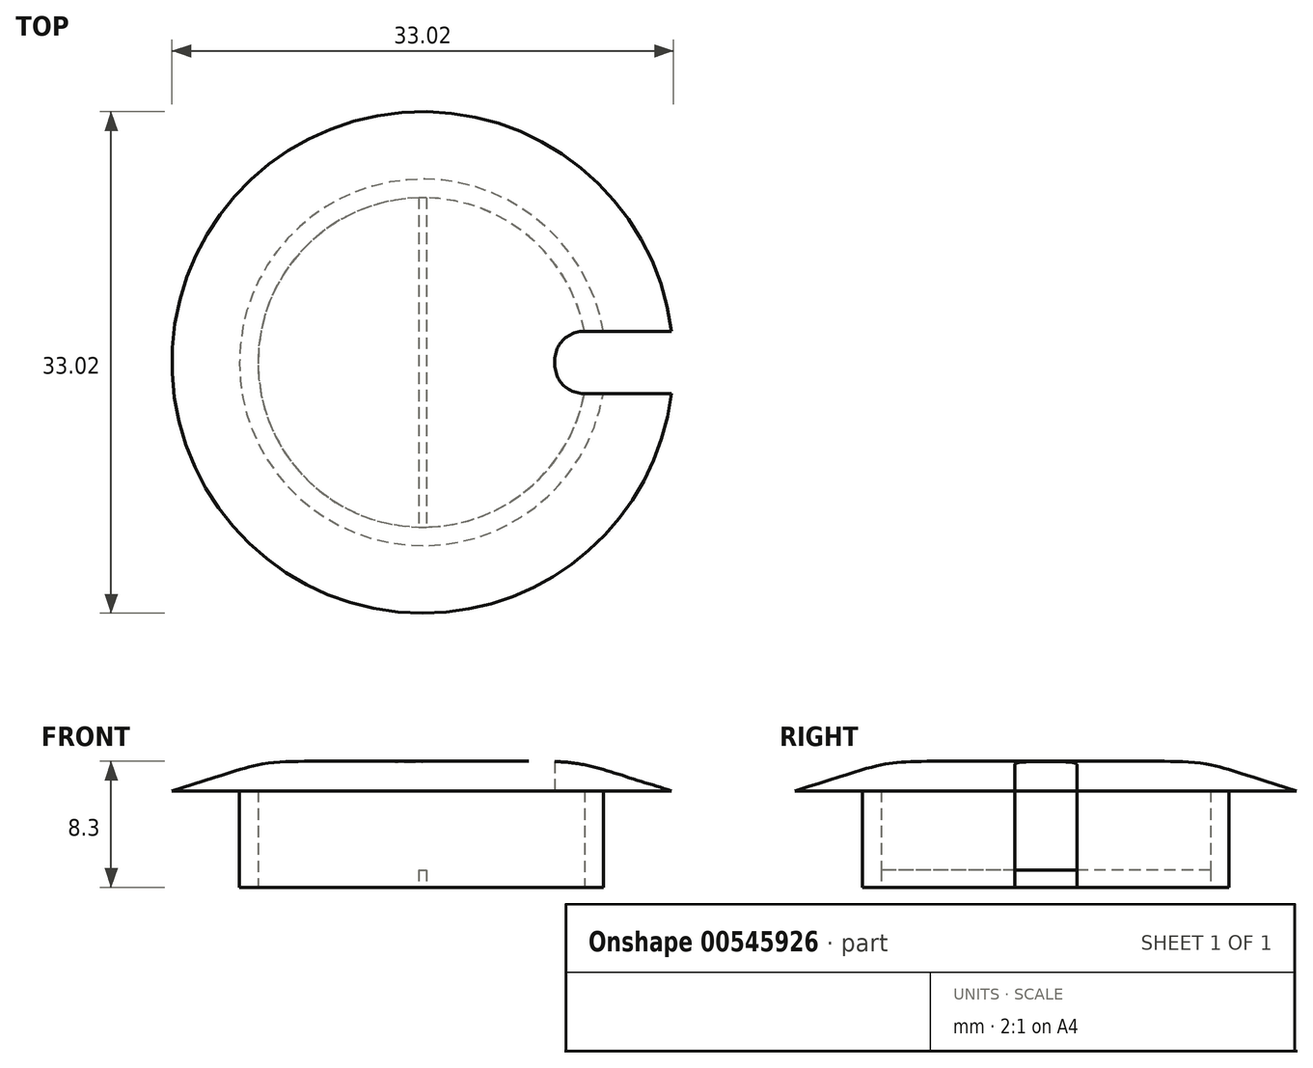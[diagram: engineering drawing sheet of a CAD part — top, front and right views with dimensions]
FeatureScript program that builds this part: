
annotation { "Feature Type Name" : "Feature", "Feature Type Description" : "" }
export const myFeature = defineFeature(function(context is Context, id is Id, definition is map)
    precondition{}
    {
        {
            var Q0;
            Q0=qCreatedBy(makeId("Top.planeOp"),FACE);
            var sketch = newSketch(context, id + "F0", { "sketchPlane" : qUnion([Q0])});
            skCircle(sketch, "E0", {"center": v(0, 0) * mm, "radius": 12.07 * mm});
            skCircle(sketch, "E1", {"center": v(0, 0) * mm, "radius": 10.85 * mm});
            skSolve(sketch);
        }
        {
            var Q0;
            Q0=makeQuery(id+"F0.imprint","IMPRINT",FACE,{"disambiguationData":[TD([[makeQuery(id+"F0.imprint","IMPRINT",EDGE,{"derivedFrom":sQuery(id+"F0.wireOp",EDGE,"E0")}),1.0]])]});
            extrude(context, id + "F1", {"entities" : qUnion([Q0]), "depth" : 6.35 * mm, "offsetDistance" : 25.4 * mm});
        }
        {
            var Q0;
            Q0=makeQuery(id+"F1.opExtrude","CAP_FACE",FACE,{"disambiguationData":[OSD([sQuery(id+"F0.wireOp",EDGE,"E0"),sQuery(id+"F0.wireOp",EDGE,"E1")])],"isStart":false});
            var sketch = newSketch(context, id + "F2", { "sketchPlane" : qUnion([Q0])});
            skCircle(sketch, "E2", {"center": v(0, 0) * mm, "radius": 15.88 * mm});
            skSolve(sketch);
        }
        {
            var Q0;
            Q0=qCreatedBy(makeId("Right.planeOp"),FACE);
            var sketch = newSketch(context, id + "F3", { "sketchPlane" : qUnion([Q0])});
            skLineSegment(sketch, "E3", {"start": v(0, 0) * mm, "end": v(0, 6.35) * mm});
            skLineSegment(sketch, "E4", {"start": v(0, 6.35) * mm, "end": v(-16.51, 6.35) * mm});
            skLineSegment(sketch, "E5", {"start": v(0, 8.26) * mm, "end": v(0, 6.35) * mm});
            skFitSpline(sketch, "E6", {"points": [v(-16.51, 6.35) * mm, v(-9.35, 8.26) * mm, v(0, 8.26) * mm], "startDerivative": vector(31.4, 9.89) * mm, "endDerivative": vector(24.38, -0.03) * mm});
            skSolve(sketch);
        }
        {
            var Q0;
            Q0=makeQuery(id+"F3.imprint","IMPRINT",FACE,{"disambiguationData":[TD([[makeQuery(id+"F3.imprint","IMPRINT",EDGE,{"derivedFrom":sQuery(id+"F3.wireOp",EDGE,"E4")}),-1.0]])]});
            var Q1;
            Q1=sQuery(id+"F3.wireOp",EDGE,"E5");
            revolve(context, id + "F4", {"operationType" : NewBodyOperationType.ADD, "entities" : qUnion([Q0]), "axis" : qUnion([Q1]), "revolveType" : RevolveType.FULL});
        }
        {
            var Q0;
            Q0=makeQuery(id+"F1.opExtrude","CAP_FACE",FACE,{"disambiguationData":[OSD([sQuery(id+"F0.wireOp",EDGE,"E0"),sQuery(id+"F0.wireOp",EDGE,"E1")])],"isStart":true});
            cPlane(context, id + "F5", {"entities" : qUnion([Q0]), "cplaneType" : CPlaneType.OFFSET, "offset" : 3.17 * mm, "oppositeDirection" : true, "width" : 152.4 * mm, "height" : 152.4 * mm});
        }
        {
            var Q0;
            Q0=qCreatedBy(id+"F5.planeOp",FACE);
            var sketch = newSketch(context, id + "F6", { "sketchPlane" : qUnion([Q0])});
            skLineSegment(sketch, "E7", {"start": v(0, 0) * mm, "end": v(8.7, 0) * mm});
            skLineSegment(sketch, "E8", {"start": v(8.7, 0) * mm, "end": v(8.7, 0.16) * mm});
            skLineSegment(sketch, "E9", {"start": v(8.7, 0) * mm, "end": v(16.5, 0) * mm});
            skLineSegment(sketch, "E10", {"start": v(16.5, 0) * mm, "end": v(16.5, 2.04) * mm});
            skLineSegment(sketch, "E11", {"start": v(16.5, 2.04) * mm, "end": v(10.59, 2.04) * mm});
            skLineSegment(sketch, "E12", {"start": v(8.7, 0) * mm, "end": v(8.7, -0.16) * mm});
            skLineSegment(sketch, "E13", {"start": v(10.59, -2.04) * mm, "end": v(16.5, -2.04) * mm});
            skLineSegment(sketch, "E14", {"start": v(16.5, -2.04) * mm, "end": v(16.5, 0) * mm});
            skPoint(sketch, "E15.visualSharp", {"position": v(8.7, -2.04) * mm});
            skArc(sketch, "E15.filletArc", {"start": v(8.7, -0.16) * mm, "mid": v(9.25, -1.5) * mm, "end": v(10.59, -2.04) * mm});
            skPoint(sketch, "E16.visualSharp", {"position": v(8.7, 2.04) * mm});
            skArc(sketch, "E16.filletArc", {"start": v(10.59, 2.04) * mm, "mid": v(9.25, 1.5) * mm, "end": v(8.7, 0.16) * mm});
            skSolve(sketch);
        }
        {
            var Q0;
            Q0=makeQuery(id+"F6.imprint","IMPRINT",FACE,{"disambiguationData":[TD([[makeQuery(id+"F6.imprint","IMPRINT",EDGE,{"derivedFrom":sQuery(id+"F6.wireOp",EDGE,"E9")}),-1.0]])]});
            var Q1;
            Q1=makeQuery(id+"F6.imprint","IMPRINT",FACE,{"disambiguationData":[TD([[makeQuery(id+"F6.imprint","IMPRINT",EDGE,{"derivedFrom":sQuery(id+"F6.wireOp",EDGE,"E8")}),-1.0]])]});
            extrude(context, id + "F7", {"entities" : qUnion([Q0, Q1]), "operationType" : NewBodyOperationType.REMOVE, "oppositeDirection" : true, "depth" : 25.4 * mm, "offsetDistance" : 25.4 * mm});
        }
        {
            var Q0;
            Q0=makeQuery(id+"F7.boolean.opBoolean","COPY",FACE,{"derivedFrom":makeQuery(id+"F7.opExtrude","CAP_FACE",FACE,{"disambiguationData":[OSD([sQuery(id+"F6.wireOp",EDGE,"E8"),sQuery(id+"F6.wireOp",EDGE,"E10"),sQuery(id+"F6.wireOp",EDGE,"E11"),sQuery(id+"F6.wireOp",EDGE,"E12"),sQuery(id+"F6.wireOp",EDGE,"E13"),sQuery(id+"F6.wireOp",EDGE,"E14"),sQuery(id+"F6.wireOp",EDGE,"E15.filletArc"),sQuery(id+"F6.wireOp",EDGE,"E16.filletArc")])],"isStart":true})});
            var sketch = newSketch(context, id + "F8", { "sketchPlane" : qUnion([Q0])});
            skLineSegment(sketch, "E17", {"start": v(10.65, 2.04) * mm, "end": v(11.9, 2.04) * mm});
            skLineSegment(sketch, "E18", {"start": v(11.9, -2.04) * mm, "end": v(10.65, -2.04) * mm});
            skLineSegment(sketch, "E19", {"start": v(10.65, -2.04) * mm, "end": v(10.65, 2.04) * mm});
            skLineSegment(sketch, "E20", {"start": v(11.9, 2.04) * mm, "end": v(12.36, 2.04) * mm});
            skLineSegment(sketch, "E21", {"start": v(12.36, 2.04) * mm, "end": v(12.36, -2.04) * mm});
            skLineSegment(sketch, "E22", {"start": v(12.36, -2.04) * mm, "end": v(11.9, -2.04) * mm});
            skSolve(sketch);
        }
        {
            var Q0;
            Q0=makeQuery(id+"F8.imprint","IMPRINT",FACE,{"disambiguationData":[TD([[makeQuery(id+"F8.imprint","IMPRINT",EDGE,{"derivedFrom":sQuery(id+"F8.wireOp",EDGE,"E17")}),-1.0]])]});
            extrude(context, id + "F9", {"entities" : qUnion([Q0]), "operationType" : NewBodyOperationType.REMOVE, "oppositeDirection" : true, "depth" : 25.4 * mm, "offsetDistance" : 25.4 * mm});
        }
        {
            var Q0;
            Q0=makeQuery(id+"F1.opExtrude","CAP_FACE",FACE,{"disambiguationData":[OSD([sQuery(id+"F0.wireOp",EDGE,"E0"),sQuery(id+"F0.wireOp",EDGE,"E1")])],"isStart":true});
            var sketch = newSketch(context, id + "F10", { "sketchPlane" : qUnion([Q0])});
            skLineSegment(sketch, "E23", {"start": v(0, -10.85) * mm, "end": v(0.25, -10.85) * mm});
            skLineSegment(sketch, "E24", {"start": v(0.25, -10.85) * mm, "end": v(0.25, 10.85) * mm});
            skLineSegment(sketch, "E25", {"start": v(0.25, 10.85) * mm, "end": v(0, 10.85) * mm});
            skLineSegment(sketch, "E26", {"start": v(0, -10.85) * mm, "end": v(-0.25, -10.85) * mm});
            skLineSegment(sketch, "E27", {"start": v(-0.25, -10.85) * mm, "end": v(-0.25, 10.85) * mm});
            skLineSegment(sketch, "E28", {"start": v(-0.25, 10.85) * mm, "end": v(0, 10.85) * mm});
            skSolve(sketch);
        }
        {
            var Q0;
            {var subQ0=makeQuery(id+"F1.opExtrude","CAP_EDGE",EDGE,{"disambiguationData":[OSD([sQuery(id+"F0.wireOp",EDGE,"E1")])],"isStart":true});var subQ2=sQuery(id+"F10.wireOp",EDGE,"E24");var subQ3=makeQuery(id+"F10.imprint","INTERSECT",VERTEX,{"disambiguationData":[OD(0.0)],"derivedFrom":[subQ0,subQ2]});Q0=makeQuery(id+"F10.imprint","IMPRINT",FACE,{"disambiguationData":[TD([[makeQuery(id+"F10.imprint","IMPRINT",EDGE,{"disambiguationData":[TD([[subQ3,-1.0]])],"derivedFrom":subQ2}),1.0]])]});}
            extrude(context, id + "F11", {"entities" : qUnion([Q0]), "operationType" : NewBodyOperationType.ADD, "oppositeDirection" : true, "depth" : 1.14 * mm, "offsetDistance" : 25.4 * mm});
        }
    });
